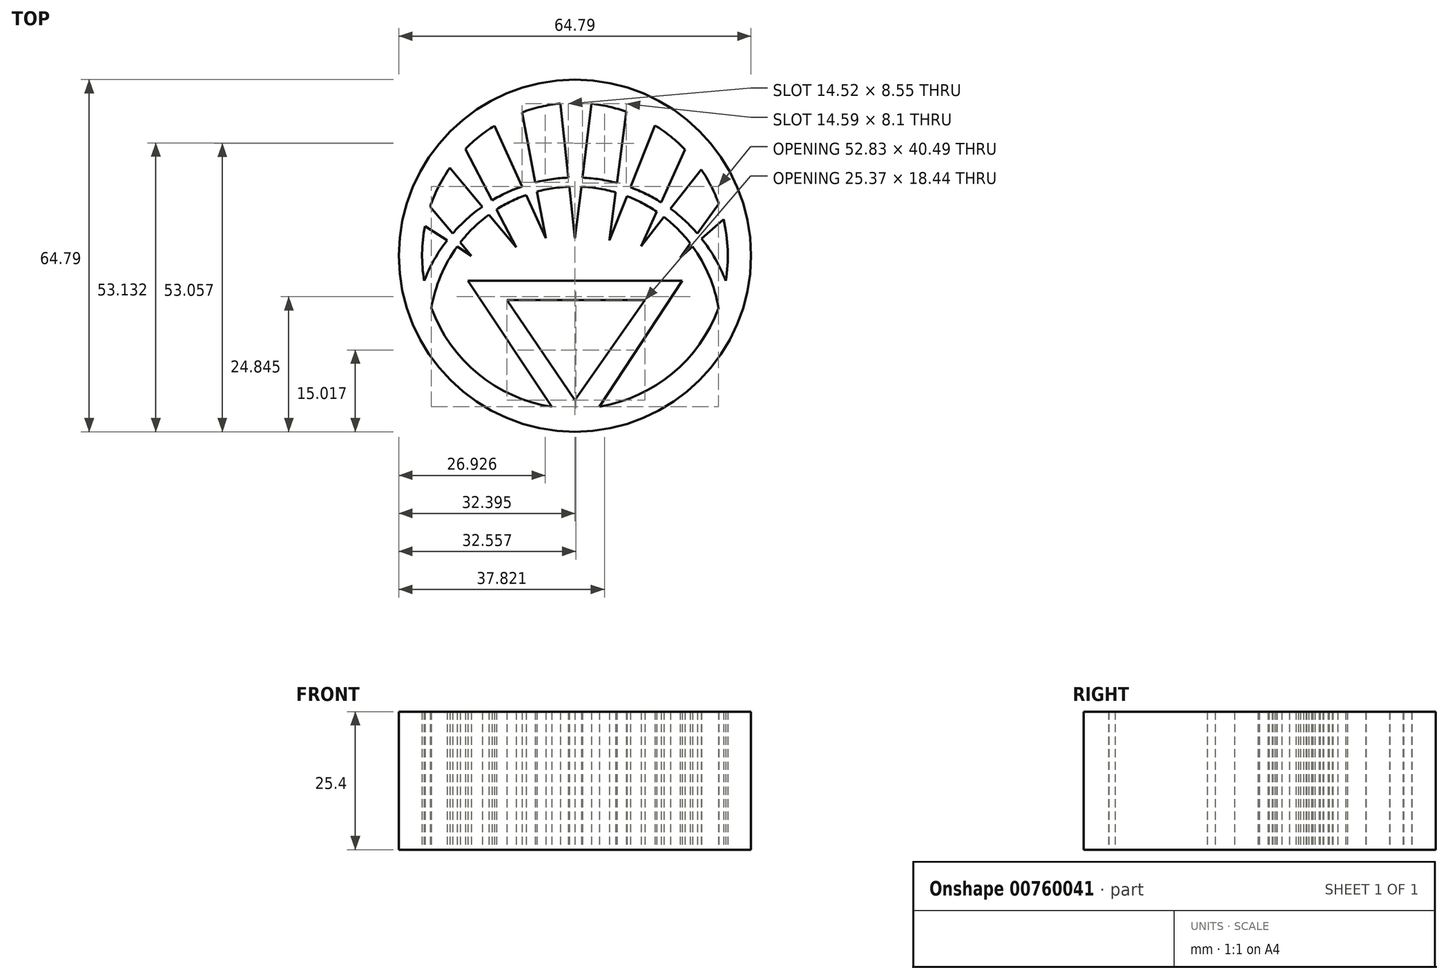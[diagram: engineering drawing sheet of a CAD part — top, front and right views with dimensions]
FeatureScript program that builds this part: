
annotation { "Feature Type Name" : "Feature", "Feature Type Description" : "" }
export const myFeature = defineFeature(function(context is Context, id is Id, definition is map)
    precondition{}
    {
        {
            var Q0;
            Q0=qCreatedBy(makeId("Top.planeOp"),FACE);
            var sketch = newSketch(context, id + "F0", { "sketchPlane" : qUnion([Q0])});
            skCircle(sketch, "E0", {"center": v(37.63, 37.53) * mm, "radius": 32.4 * mm});
            skArc(sketch, "E1", {"start": v(42.15, 9.77) * mm, "mid": v(55.55, 15.85) * mm, "end": v(64.04, 27.86) * mm});
            skArc(sketch, "E2", {"start": v(64.04, 27.86) * mm, "mid": v(62.32, 33.82) * mm, "end": v(59.27, 39.22) * mm});
            skLineSegment(sketch, "E3", {"start": v(37.62, 10.93) * mm, "end": v(25.1, 29.36) * mm});
            skLineSegment(sketch, "E4", {"start": v(25.1, 29.36) * mm, "end": v(50.47, 29.36) * mm});
            skLineSegment(sketch, "E5", {"start": v(50.47, 29.36) * mm, "end": v(37.62, 10.93) * mm});
            skLineSegment(sketch, "E6", {"start": v(33.35, 9.73) * mm, "end": v(17.94, 32.89) * mm});
            skLineSegment(sketch, "E7", {"start": v(17.94, 32.89) * mm, "end": v(57.34, 32.89) * mm});
            skLineSegment(sketch, "E8", {"start": v(57.34, 32.89) * mm, "end": v(42.15, 9.77) * mm});
            skLineSegment(sketch, "E9", {"start": v(40.68, 65.48) * mm, "end": v(39, 51.88) * mm});
            skLineSegment(sketch, "E10", {"start": v(37.63, 40.74) * mm, "end": v(36.6, 50.22) * mm});
            skArc(sketch, "E11", {"start": v(65.37, 32.89) * mm, "mid": v(63.44, 36.94) * mm, "end": v(60.92, 40.66) * mm});
            skLineSegment(sketch, "E12", {"start": v(27.88, 63.9) * mm, "end": v(30.32, 51) * mm});
            skLineSegment(sketch, "E13", {"start": v(32.26, 40.74) * mm, "end": v(28.63, 48.69) * mm});
            skLineSegment(sketch, "E14", {"start": v(17.46, 57.13) * mm, "end": v(22.34, 47.68) * mm});
            skLineSegment(sketch, "E15", {"start": v(26.79, 39.07) * mm, "end": v(21.8, 45.06) * mm});
            skLineSegment(sketch, "E16", {"start": v(10.99, 46.54) * mm, "end": v(15.12, 41.6) * mm});
            skLineSegment(sketch, "E17", {"start": v(18.58, 37.47) * mm, "end": v(15.94, 39.17) * mm});
            skLineSegment(sketch, "E18", {"start": v(47.1, 64) * mm, "end": v(45.35, 50.9) * mm});
            skLineSegment(sketch, "E19", {"start": v(43.95, 40.36) * mm, "end": v(47.17, 48.48) * mm});
            skLineSegment(sketch, "E20", {"start": v(57.88, 57.04) * mm, "end": v(53.47, 47.34) * mm});
            skLineSegment(sketch, "E21", {"start": v(49.8, 39.29) * mm, "end": v(54, 44.64) * mm});
            skLineSegment(sketch, "E22", {"start": v(64.09, 47.06) * mm, "end": v(60.14, 41.6) * mm});
            skLineSegment(sketch, "E23", {"start": v(56.95, 37.2) * mm, "end": v(59.27, 39.22) * mm});
            skArc(sketch, "E24.trimOffspring", {"start": v(11.21, 27.87) * mm, "mid": v(19.8, 15.77) * mm, "end": v(33.35, 9.73) * mm});
            skArc(sketch, "E25.trimOffspring", {"start": v(10.04, 42.98) * mm, "mid": v(9.5, 37.94) * mm, "end": v(9.89, 32.89) * mm});
            skArc(sketch, "E26.trimOffspring", {"start": v(14.61, 53.7) * mm, "mid": v(12.54, 50.24) * mm, "end": v(10.99, 46.54) * mm});
            skArc(sketch, "E27.trimOffspring", {"start": v(22.82, 61.44) * mm, "mid": v(20, 59.45) * mm, "end": v(17.46, 57.13) * mm});
            skArc(sketch, "E28.trimOffspring", {"start": v(34.96, 65.52) * mm, "mid": v(31.37, 64.94) * mm, "end": v(27.88, 63.9) * mm});
            skArc(sketch, "E29.trimOffspring", {"start": v(47.1, 64) * mm, "mid": v(43.93, 64.93) * mm, "end": v(40.68, 65.48) * mm});
            skArc(sketch, "E30.trimOffspring", {"start": v(57.88, 57.04) * mm, "mid": v(55.24, 59.45) * mm, "end": v(52.33, 61.5) * mm});
            skArc(sketch, "E31.trimOffspring", {"start": v(64.09, 47.06) * mm, "mid": v(62.67, 50.32) * mm, "end": v(60.86, 53.37) * mm});
            skArc(sketch, "E32.trimOffspring", {"start": v(65.37, 32.89) * mm, "mid": v(65.73, 38.56) * mm, "end": v(64.95, 44.19) * mm});
            skLineSegment(sketch, "E33.trimOffspring", {"start": v(14.1, 40.36) * mm, "end": v(10.04, 42.98) * mm});
            skArc(sketch, "E34.trimOffspring", {"start": v(14.1, 40.36) * mm, "mid": v(11.72, 36.78) * mm, "end": v(9.89, 32.89) * mm});
            skLineSegment(sketch, "E35.trimOffspring", {"start": v(16.51, 39.94) * mm, "end": v(18.58, 37.47) * mm});
            skArc(sketch, "E36.trimOffspring", {"start": v(15.94, 39.17) * mm, "mid": v(12.92, 33.8) * mm, "end": v(11.21, 27.87) * mm});
            skArc(sketch, "E37.trimOffspring", {"start": v(20.57, 46.53) * mm, "mid": v(17.7, 44.24) * mm, "end": v(15.12, 41.6) * mm});
            skLineSegment(sketch, "E38.trimOffspring", {"start": v(20.57, 46.53) * mm, "end": v(14.61, 53.7) * mm});
            skArc(sketch, "E39.trimOffspring", {"start": v(21.8, 45.06) * mm, "mid": v(18.98, 42.68) * mm, "end": v(16.51, 39.94) * mm});
            skLineSegment(sketch, "E40.trimOffspring", {"start": v(23.2, 46.02) * mm, "end": v(26.79, 39.07) * mm});
            skArc(sketch, "E41.trimOffspring", {"start": v(27.9, 50.28) * mm, "mid": v(25.06, 49.12) * mm, "end": v(22.34, 47.68) * mm});
            skLineSegment(sketch, "E42.trimOffspring", {"start": v(27.9, 50.28) * mm, "end": v(22.82, 61.44) * mm});
            skArc(sketch, "E43.trimOffspring", {"start": v(28.63, 48.69) * mm, "mid": v(25.84, 47.5) * mm, "end": v(23.2, 46.02) * mm});
            skLineSegment(sketch, "E44.trimOffspring", {"start": v(30.64, 49.31) * mm, "end": v(32.26, 40.74) * mm});
            skArc(sketch, "E45.trimOffspring", {"start": v(36.43, 51.89) * mm, "mid": v(33.35, 51.6) * mm, "end": v(30.32, 51) * mm});
            skLineSegment(sketch, "E46.trimOffspring", {"start": v(36.43, 51.89) * mm, "end": v(34.96, 65.52) * mm});
            skArc(sketch, "E47.trimOffspring", {"start": v(36.6, 50.22) * mm, "mid": v(33.6, 49.94) * mm, "end": v(30.64, 49.31) * mm});
            skLineSegment(sketch, "E48.trimOffspring", {"start": v(38.8, 50.21) * mm, "end": v(37.63, 40.74) * mm});
            skArc(sketch, "E49.trimOffspring", {"start": v(45.35, 50.9) * mm, "mid": v(42.2, 51.56) * mm, "end": v(39, 51.88) * mm});
            skLineSegment(sketch, "E50.trimOffspring", {"start": v(45.12, 49.17) * mm, "end": v(43.95, 40.36) * mm});
            skArc(sketch, "E51.trimOffspring", {"start": v(45.12, 49.17) * mm, "mid": v(42, 49.88) * mm, "end": v(38.8, 50.21) * mm});
            skLineSegment(sketch, "E52.trimOffspring", {"start": v(47.81, 50.11) * mm, "end": v(52.33, 61.5) * mm});
            skArc(sketch, "E53.trimOffspring", {"start": v(53.47, 47.34) * mm, "mid": v(50.71, 48.88) * mm, "end": v(47.81, 50.11) * mm});
            skLineSegment(sketch, "E54.trimOffspring", {"start": v(52.68, 45.6) * mm, "end": v(49.8, 39.29) * mm});
            skArc(sketch, "E55.trimOffspring", {"start": v(52.68, 45.6) * mm, "mid": v(50, 47.2) * mm, "end": v(47.17, 48.48) * mm});
            skLineSegment(sketch, "E56.trimOffspring", {"start": v(55.2, 46.16) * mm, "end": v(60.86, 53.37) * mm});
            skArc(sketch, "E57.trimOffspring", {"start": v(60.14, 41.6) * mm, "mid": v(57.8, 44.02) * mm, "end": v(55.2, 46.16) * mm});
            skLineSegment(sketch, "E58.trimOffspring", {"start": v(58.84, 39.8) * mm, "end": v(56.95, 37.2) * mm});
            skArc(sketch, "E59.trimOffspring", {"start": v(58.84, 39.8) * mm, "mid": v(56.58, 42.38) * mm, "end": v(54, 44.64) * mm});
            skLineSegment(sketch, "E60.trimOffspring", {"start": v(60.92, 40.66) * mm, "end": v(64.95, 44.19) * mm});
            skSolve(sketch);
        }
        {
            var Q0;
            Q0=makeQuery(id+"F0.imprint","IMPRINT",FACE,{"disambiguationData":[TD([[makeQuery(id+"F0.imprint","IMPRINT",EDGE,{"derivedFrom":sQuery(id+"F0.wireOp",EDGE,"E0")}),1.0]])]});
            extrude(context, id + "F1", {"entities" : qUnion([Q0]), "depth" : 25.4 * mm, "offsetDistance" : 25.4 * mm});
        }
    });
